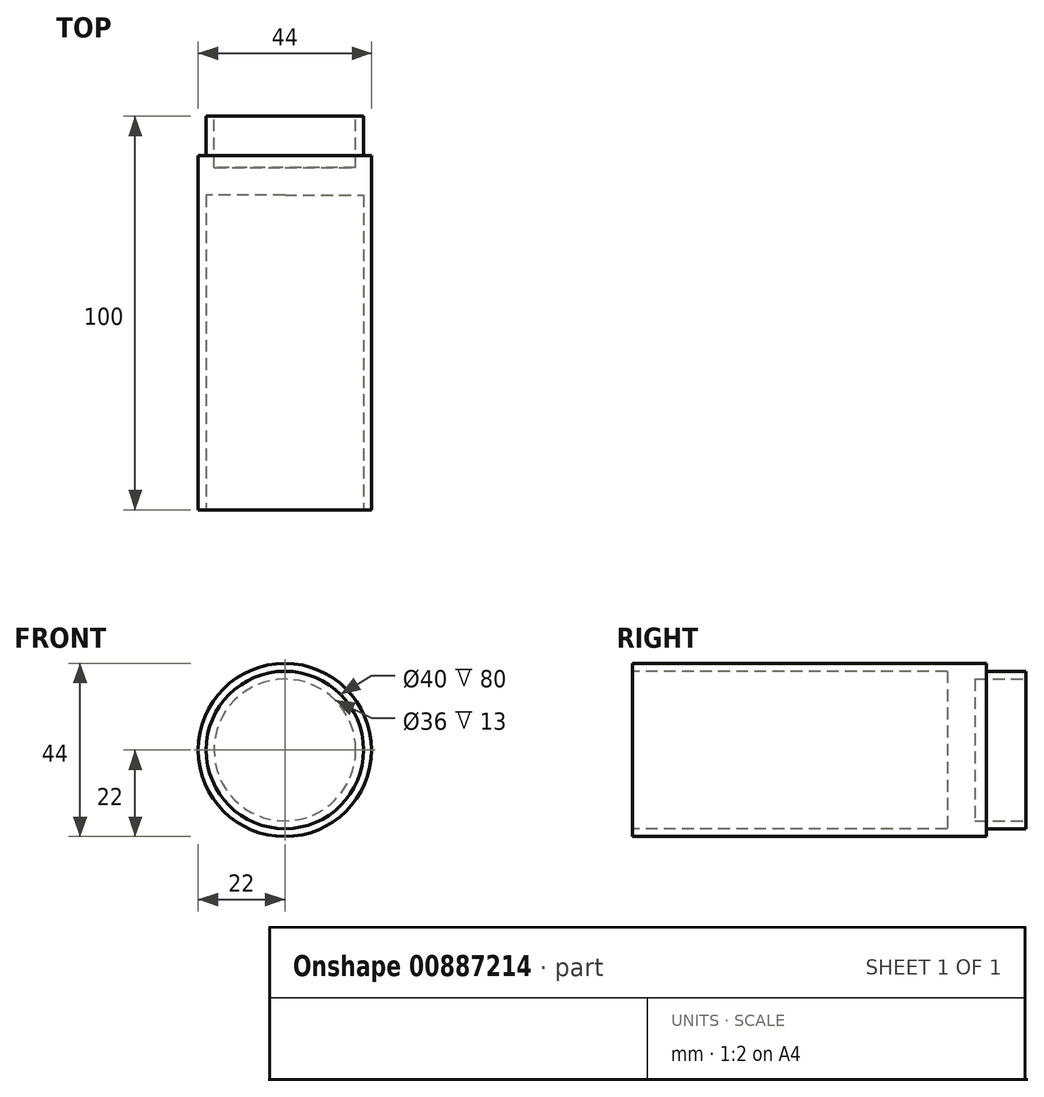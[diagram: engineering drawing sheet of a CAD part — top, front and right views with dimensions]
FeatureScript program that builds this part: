
annotation { "Feature Type Name" : "Feature", "Feature Type Description" : "" }
export const myFeature = defineFeature(function(context is Context, id is Id, definition is map)
    precondition{}
    {
        {
            var Q0;
            Q0=qCreatedBy(makeId("Right.planeOp"),FACE);
            var sketch = newSketch(context, id + "F0", { "sketchPlane" : qUnion([Q0])});
            skLineSegment(sketch, "E0", {"start": v(-7.5, 0) * mm, "end": v(89.13, 0) * mm});
            skLineSegment(sketch, "E1.bottom", {"start": v(-45, -20) * mm, "end": v(45, -20) * mm});
            skLineSegment(sketch, "E1.top", {"start": v(-45, -22) * mm, "end": v(45, -22) * mm});
            skLineSegment(sketch, "E1.left", {"start": v(-45, -20) * mm, "end": v(-45, -22) * mm});
            skLineSegment(sketch, "E1.right", {"start": v(45, -20) * mm, "end": v(45, -22) * mm});
            skPoint(sketch, "E1.middle", {"position": v(0, -21) * mm});
            skSolve(sketch);
        }
        {
            var Q0;
            Q0=makeQuery(id+"F0.imprint","IMPRINT",FACE,{"disambiguationData":[TD([[makeQuery(id+"F0.imprint","IMPRINT",EDGE,{"derivedFrom":sQuery(id+"F0.wireOp",EDGE,"E1.bottom")}),-1.0]])]});
            var Q1;
            Q1=sQuery(id+"F0.wireOp",EDGE,"E0");
            revolve(context, id + "F1", {"entities" : qUnion([Q0]), "axis" : qUnion([Q1]), "revolveType" : RevolveType.FULL});
        }
        {
            var Q0;
            Q0=makeQuery(id+"F1.opRevolve","SWEPT_FACE",FACE,{"disambiguationData":[OSD([sQuery(id+"F0.wireOp",EDGE,"E1.right")])]});
            var sketch = newSketch(context, id + "F2", { "sketchPlane" : qUnion([Q0])});
            skCircle(sketch, "E2", {"center": v(0, 0) * mm, "radius": 20 * mm});
            skSolve(sketch);
        }
        {
            var Q0;
            Q0 = qSketchRegion(id + "F2", true);
            extrude(context, id + "F3", {"entities" : qUnion([Q0]), "operationType" : NewBodyOperationType.ADD, "endBound" : BoundingType.SYMMETRIC, "depth" : 20 * mm, "offsetDistance" : 25 * mm});
        }
        {
            var Q0;
            Q0=makeQuery(id+"F3.opExtrude","CAP_FACE",FACE,{"disambiguationData":[OSD([sQuery(id+"F2.wireOp",EDGE,"E2")])],"isStart":false});
            var sketch = newSketch(context, id + "F4", { "sketchPlane" : qUnion([Q0])});
            skCircle(sketch, "E3", {"center": v(0, 0) * mm, "radius": 18 * mm});
            skSolve(sketch);
        }
        {
            var Q0;
            Q0 = qSketchRegion(id + "F4", true);
            extrude(context, id + "F5", {"entities" : qUnion([Q0]), "operationType" : NewBodyOperationType.REMOVE, "oppositeDirection" : true, "depth" : 13 * mm, "offsetDistance" : 25 * mm});
        }
    });
